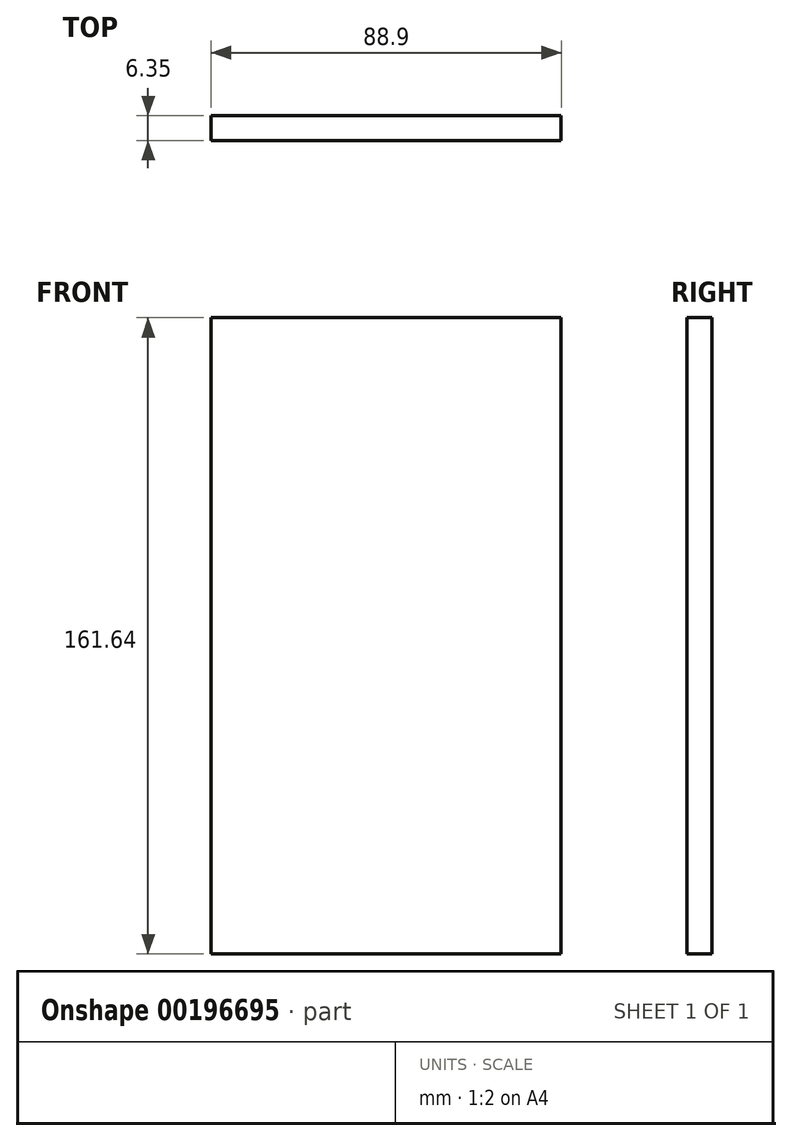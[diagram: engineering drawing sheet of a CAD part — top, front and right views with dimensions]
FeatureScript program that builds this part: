
annotation { "Feature Type Name" : "Feature", "Feature Type Description" : "" }
export const myFeature = defineFeature(function(context is Context, id is Id, definition is map)
    precondition{}
    {
        {
            var Q0;
            Q0=qCreatedBy(makeId("Front.planeOp"),FACE);
            var sketch = newSketch(context, id + "F0", { "sketchPlane" : qUnion([Q0])});
            skLineSegment(sketch, "E0.bottom", {"start": v(-39.3, 119.4) * mm, "end": v(49.6, 119.4) * mm});
            skLineSegment(sketch, "E0.top", {"start": v(-39.3, -42.25) * mm, "end": v(49.6, -42.25) * mm});
            skLineSegment(sketch, "E0.left", {"start": v(-39.3, 119.4) * mm, "end": v(-39.3, -42.25) * mm});
            skLineSegment(sketch, "E0.right", {"start": v(49.6, 119.4) * mm, "end": v(49.6, -42.25) * mm});
            skSolve(sketch);
        }
        {
            var Q0;
            Q0=makeQuery(id+"F0.imprint","IMPRINT",FACE,{"disambiguationData":[TD([[makeQuery(id+"F0.imprint","IMPRINT",EDGE,{"derivedFrom":sQuery(id+"F0.wireOp",EDGE,"E0.bottom")}),-1.0]])]});
            extrude(context, id + "F1", {"entities" : qUnion([Q0]), "depth" : 6.35 * mm});
        }
    });
